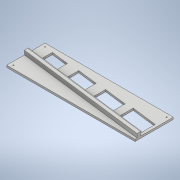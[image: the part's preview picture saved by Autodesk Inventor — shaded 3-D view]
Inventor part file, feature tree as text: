
AUTODESK INVENTOR PART (.ipt)
format: ipt  version: 2020 (Build 240168000, 168)  size: 205,824 bytes
history: native  units: mm
features: sketch x6, extrude x3, other x1, sweep x1, hole x1
ambient origin geometry x8: Origin, YZ Plane, XZ Plane, XY Plane, X Axis, Y Axis, Z Axis, Center Point
bodies: Body1 (feature_tree)
feature tree (12):
  other  "Твердое тело1"
  extrude  "Выдавливание1"  Depth=3.0mm TaperAngle=0.0deg
  extrude  "Выдавливание2"  Depth=6.0mm TaperAngle=0.0deg
  extrude  "Выдавливание3"  Depth=5.0mm TaperAngle=0.0deg
  sweep  "Сдвиг1"
  hole  "Отверстие2"  [1 undecoded]
  sketch  "Эскиз1"
  sketch  "Эскиз2"
  sketch  "Эскиз3"
  sketch  "Эскиз5"
  sketch  "Эскиз6"
  sketch  "3D эскиз1"
note: 1 required parameter value undecoded (feature->parameter linkage not recoverable at this tier; creation-order binding heuristic only, values carry confidence <= 0.55)
